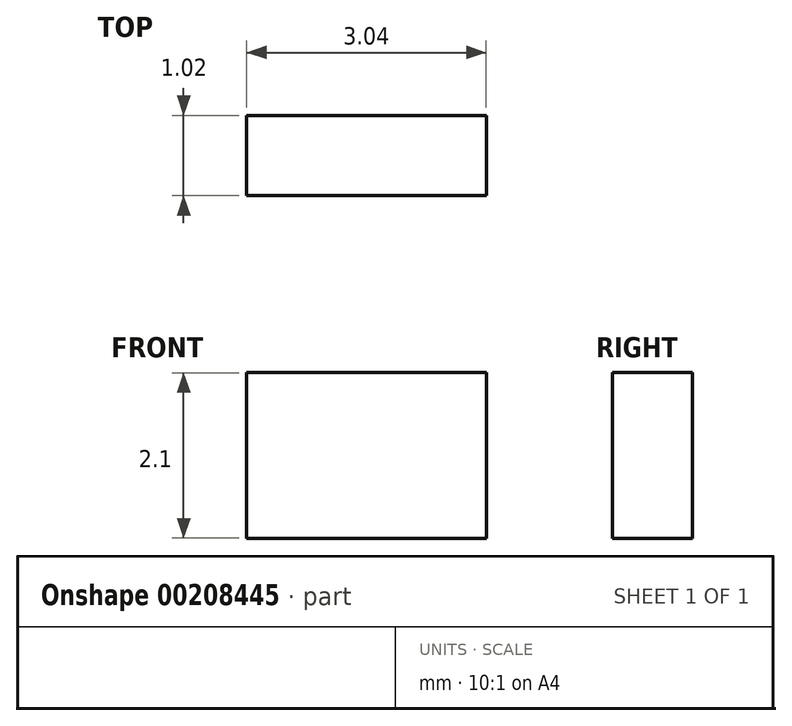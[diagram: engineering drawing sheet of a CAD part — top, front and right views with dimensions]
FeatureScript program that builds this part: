
annotation { "Feature Type Name" : "Feature", "Feature Type Description" : "" }
export const myFeature = defineFeature(function(context is Context, id is Id, definition is map)
    precondition{}
    {
        {
            var Q0;
            Q0=qCreatedBy(makeId("Front.planeOp"),FACE);
            var sketch = newSketch(context, id + "F0", { "sketchPlane" : qUnion([Q0])});
            skLineSegment(sketch, "E0.bottom", {"start": v(1.52, 1.05) * mm, "end": v(-1.52, 1.05) * mm});
            skLineSegment(sketch, "E0.top", {"start": v(1.52, -1.05) * mm, "end": v(-1.52, -1.05) * mm});
            skLineSegment(sketch, "E0.left", {"start": v(1.52, 1.05) * mm, "end": v(1.52, -1.05) * mm});
            skLineSegment(sketch, "E0.right", {"start": v(-1.52, 1.05) * mm, "end": v(-1.52, -1.05) * mm});
            skPoint(sketch, "E0.middle", {"position": v(0, 0) * mm});
            skSolve(sketch);
        }
        {
            var Q0;
            Q0=qSketchRegion(id+"F0",true);
            extrude(context, id + "F1", {"entities" : qUnion([Q0]), "depth" : 1.02 * mm});
        }
    });
